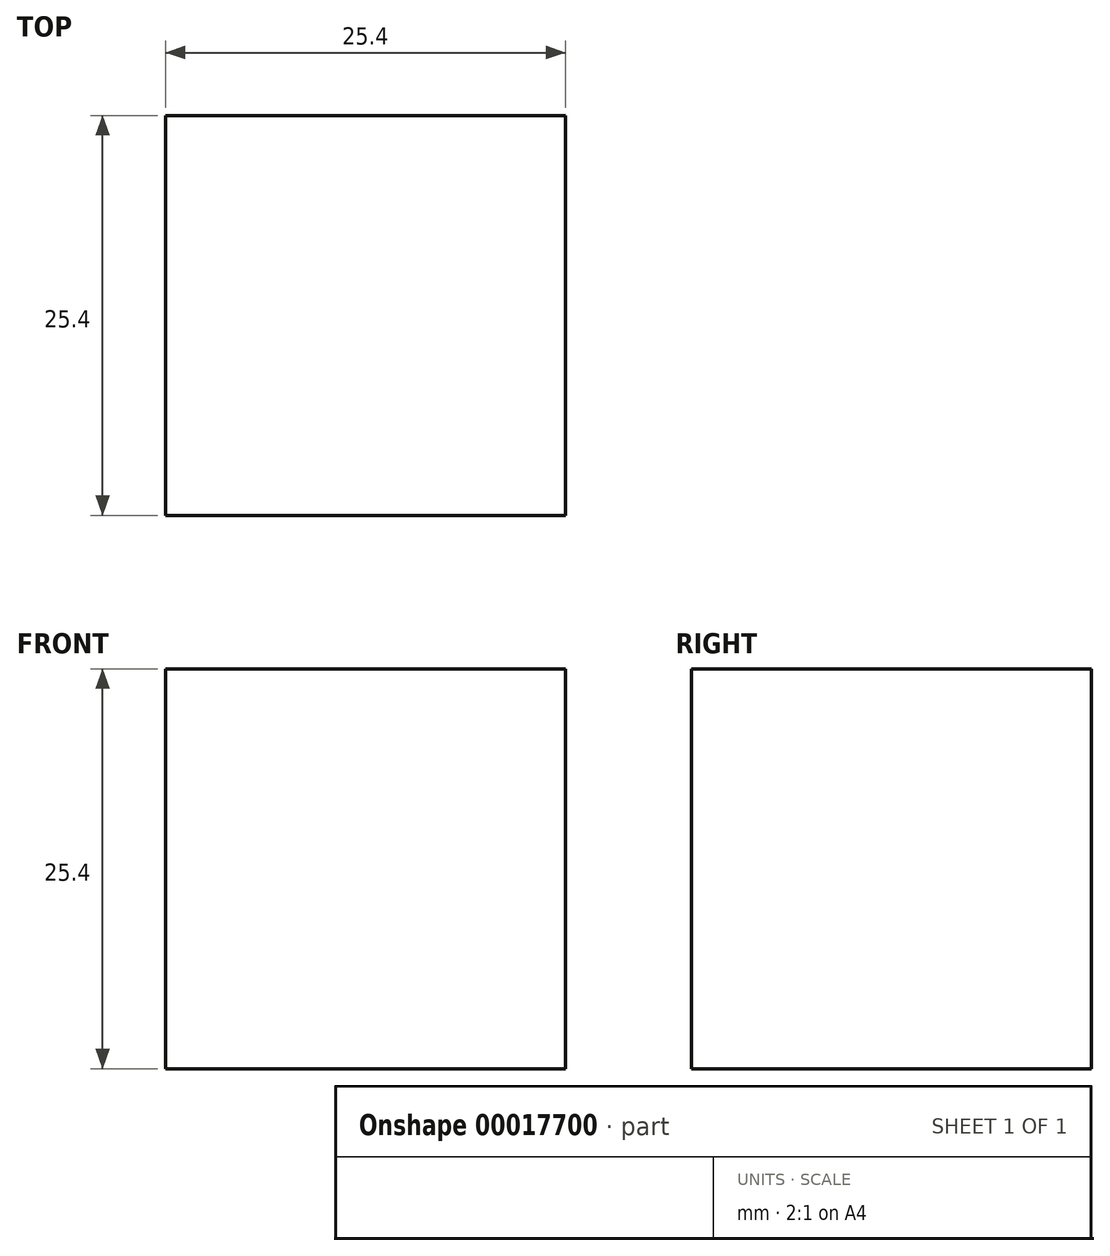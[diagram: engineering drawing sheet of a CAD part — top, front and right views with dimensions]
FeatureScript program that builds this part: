
annotation { "Feature Type Name" : "Feature", "Feature Type Description" : "" }
export const myFeature = defineFeature(function(context is Context, id is Id, definition is map)
    precondition{}
    {
        {
            var Q0;
            Q0=qCreatedBy(makeId("Front.planeOp"),FACE);
            var sketch = newSketch(context, id + "F0", { "sketchPlane" : qUnion([Q0])});
            skLineSegment(sketch, "E0.rect.bottom", {"start": v(12.7, 12.7) * mm, "end": v(-12.7, 12.7) * mm});
            skLineSegment(sketch, "E0.rect.top", {"start": v(12.7, -12.7) * mm, "end": v(-12.7, -12.7) * mm});
            skLineSegment(sketch, "E0.rect.left", {"start": v(12.7, 12.7) * mm, "end": v(12.7, -12.7) * mm});
            skLineSegment(sketch, "E0.rect.right", {"start": v(-12.7, 12.7) * mm, "end": v(-12.7, -12.7) * mm});
            skPoint(sketch, "E0.rect.middle", {"position": v(0, 0) * mm});
            skSolve(sketch);
        }
        {
            var Q0;
            Q0 = qSketchRegion(id + "F0", true);
            extrude(context, id + "F1", {"entities" : qUnion([Q0]), "endBound" : BoundingType.SYMMETRIC, "depth" : 25.4 * mm});
        }
    });
